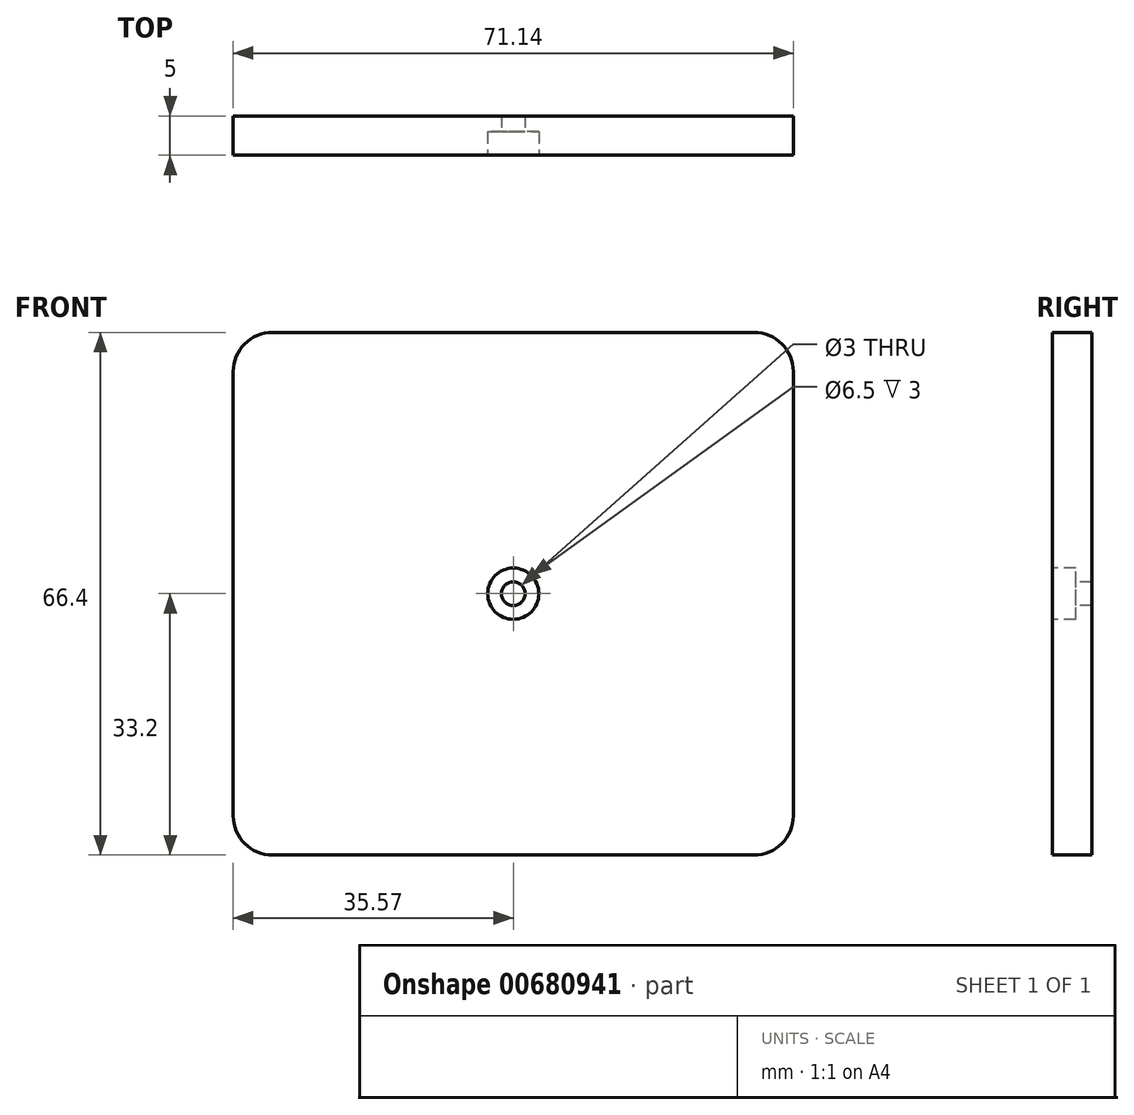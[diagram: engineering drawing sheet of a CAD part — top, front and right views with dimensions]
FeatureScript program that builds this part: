
annotation { "Feature Type Name" : "Feature", "Feature Type Description" : "" }
export const myFeature = defineFeature(function(context is Context, id is Id, definition is map)
    precondition{}
    {
        {
            var Q0;
            Q0=qCreatedBy(makeId("Front.planeOp"),FACE);
            var sketch = newSketch(context, id + "F0", { "sketchPlane" : qUnion([Q0])});
            skLineSegment(sketch, "E0.bottom", {"start": v(-35.57, 33.2) * mm, "end": v(35.57, 33.2) * mm});
            skLineSegment(sketch, "E0.top", {"start": v(-35.57, -33.2) * mm, "end": v(35.57, -33.2) * mm});
            skLineSegment(sketch, "E0.left", {"start": v(-35.57, 33.2) * mm, "end": v(-35.57, -33.2) * mm});
            skLineSegment(sketch, "E0.right", {"start": v(35.57, 33.2) * mm, "end": v(35.57, -33.2) * mm});
            skPoint(sketch, "E0.middle", {"position": v(0, 0) * mm});
            skSolve(sketch);
        }
        {
            var Q0;
            Q0 = qSketchRegion(id + "F0", true);
            extrude(context, id + "F1", {"entities" : qUnion([Q0]), "depth" : 5 * mm, "offsetDistance" : 25 * mm});
        }
        {
            var Q0;
            Q0=makeQuery(id+"F1.opExtrude","CAP_FACE",FACE,{"disambiguationData":[OSD([sQuery(id+"F0.wireOp",EDGE,"E0.bottom"),sQuery(id+"F0.wireOp",EDGE,"E0.top"),sQuery(id+"F0.wireOp",EDGE,"E0.left"),sQuery(id+"F0.wireOp",EDGE,"E0.right")])],"isStart":false});
            var sketch = newSketch(context, id + "F2", { "sketchPlane" : qUnion([Q0])});
            skPoint(sketch, "E1", {"position": v(0, 0) * mm});
            skSolve(sketch);
        }
        {
            var Q0;
            Q0=sQuery(id+"F2.wireOp",VERTEX,"E1");
            var Q1;
            Q1=makeQuery(id+"F1.opExtrude","SWEPT_BODY",BODY,{"disambiguationData":[OSD([sQuery(id+"F0.wireOp",EDGE,"E0.bottom"),sQuery(id+"F0.wireOp",EDGE,"E0.top"),sQuery(id+"F0.wireOp",EDGE,"E0.left"),sQuery(id+"F0.wireOp",EDGE,"E0.right")])]});
            hole(context, id + "F3", {"style" : HoleStyle.C_BORE, "endStyle" : HoleEndStyle.THROUGH, "holeDiameter" : 3 * mm, "cBoreDiameter" : 6.5 * mm, "cBoreDepth" : 3 * mm, "majorDiameter" : 5 * mm, "isTappedThrough" : true, "tappedDepth" : 12 * mm, "tapClearance" : 3, "locations" : qUnion([Q0]), "scope" : qUnion([Q1])});
        }
        {
            var Q0;
            Q0=makeQuery(id+"F1.opExtrude","SWEPT_EDGE",EDGE,{"disambiguationData":[OSD([sQuery(id+"F0.wireOp",EDGE,"E0.bottom"),sQuery(id+"F0.wireOp",EDGE,"E0.right")])]});
            var Q1;
            Q1=makeQuery(id+"F1.opExtrude","SWEPT_EDGE",EDGE,{"disambiguationData":[OSD([sQuery(id+"F0.wireOp",EDGE,"E0.bottom"),sQuery(id+"F0.wireOp",EDGE,"E0.left")])]});
            var Q2;
            Q2=makeQuery(id+"F1.opExtrude","SWEPT_EDGE",EDGE,{"disambiguationData":[OSD([sQuery(id+"F0.wireOp",EDGE,"E0.top"),sQuery(id+"F0.wireOp",EDGE,"E0.right")])]});
            var Q3;
            Q3=makeQuery(id+"F1.opExtrude","SWEPT_EDGE",EDGE,{"disambiguationData":[OSD([sQuery(id+"F0.wireOp",EDGE,"E0.top"),sQuery(id+"F0.wireOp",EDGE,"E0.left")])]});
            fillet(context, id + "F4", {"entities" : qUnion([Q0, Q1, Q2, Q3]), "radius" : 5 * mm, "tangentPropagation" : true, "allowEdgeOverflow" : false});
        }
    });
